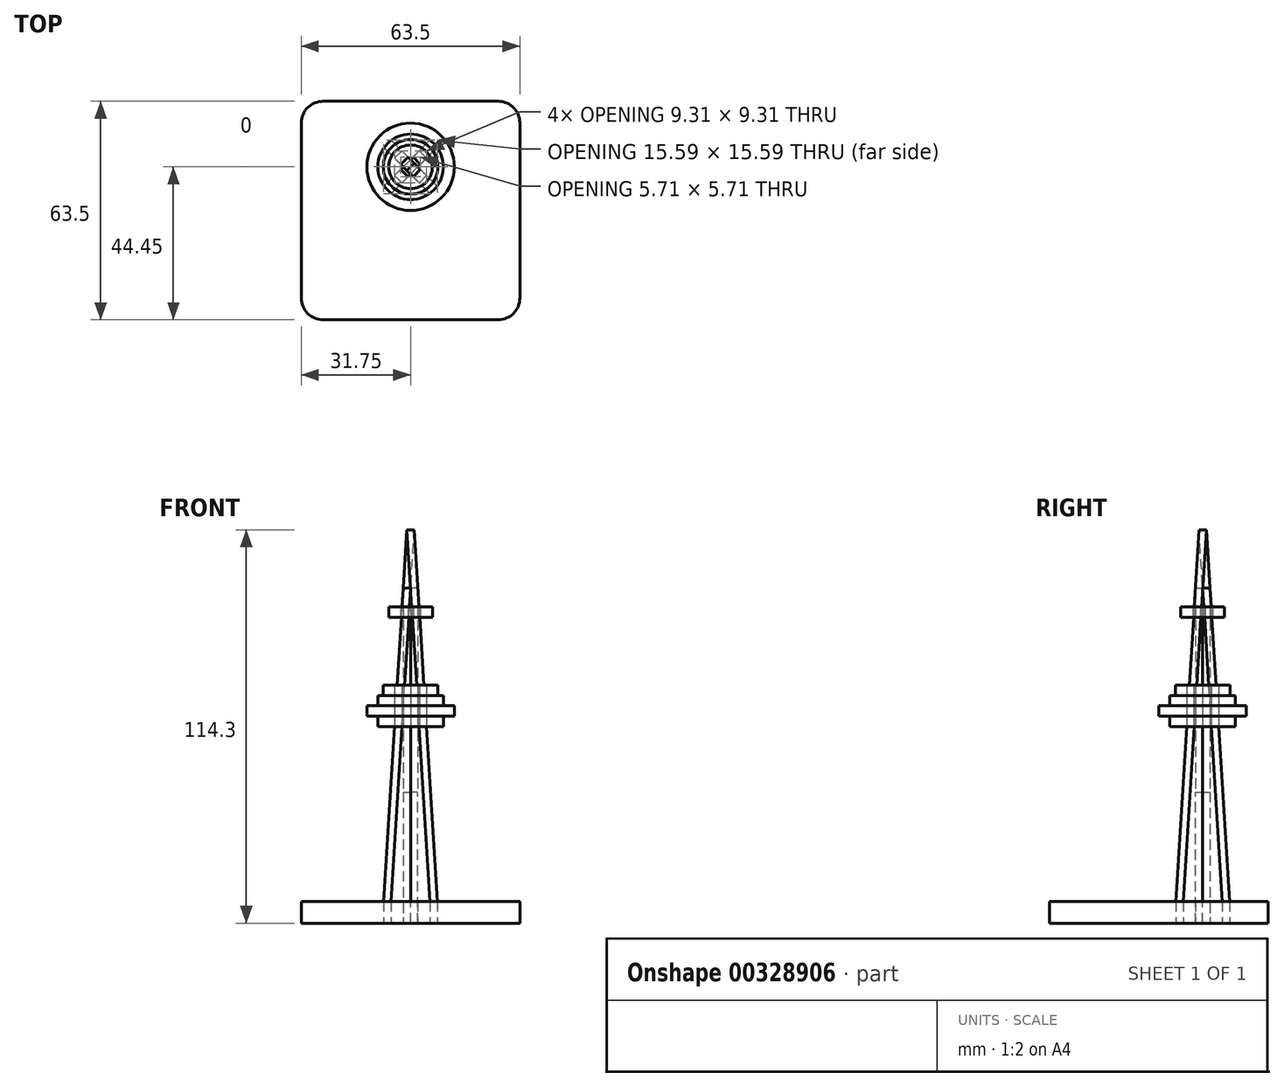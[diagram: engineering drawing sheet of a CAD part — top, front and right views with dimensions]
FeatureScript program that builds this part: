
annotation { "Feature Type Name" : "Feature", "Feature Type Description" : "" }
export const myFeature = defineFeature(function(context is Context, id is Id, definition is map)
    precondition{}
    {
        {
            var Q0;
            Q0=qCreatedBy(makeId("Top.planeOp"),FACE);
            var sketch = newSketch(context, id + "F0", { "sketchPlane" : qUnion([Q0])});
            skLineSegment(sketch, "E0", {"start": v(-7.8, 5.67) * mm, "end": v(5.67, -7.8) * mm});
            skLineSegment(sketch, "E1", {"start": v(5.67, -7.8) * mm, "end": v(7.8, -5.67) * mm});
            skLineSegment(sketch, "E2", {"start": v(7.8, -5.67) * mm, "end": v(-5.67, 7.8) * mm});
            skLineSegment(sketch, "E3", {"start": v(-7.8, 5.67) * mm, "end": v(-5.67, 7.8) * mm});
            skLineSegment(sketch, "E4", {"start": v(-7.8, 5.67) * mm, "end": v(7.8, -5.67) * mm, "construction": true});
            skLineSegment(sketch, "E5", {"start": v(-5.67, 7.8) * mm, "end": v(5.67, -7.8) * mm, "construction": true});
            skPoint(sketch, "E6", {"position": v(0, 0) * mm});
            skLineSegment(sketch, "E7", {"start": v(0, 12.63) * mm, "end": v(0, 0) * mm, "construction": true});
            skLineSegment(sketch, "E8.MirrorCS", {"start": v(-5.67, -7.8) * mm, "end": v(-7.8, -5.67) * mm});
            skLineSegment(sketch, "E9.MirrorCS", {"start": v(7.8, 5.67) * mm, "end": v(-5.67, -7.8) * mm});
            skLineSegment(sketch, "E10.MirrorCS", {"start": v(-7.8, -5.67) * mm, "end": v(5.67, 7.8) * mm});
            skLineSegment(sketch, "E11.MirrorCS", {"start": v(7.8, 5.67) * mm, "end": v(5.67, 7.8) * mm});
            skLineSegment(sketch, "E12.MirrorCS", {"start": v(5.67, 7.8) * mm, "end": v(-5.67, -7.8) * mm, "construction": true});
            skLineSegment(sketch, "E13.MirrorCS", {"start": v(7.8, 5.67) * mm, "end": v(-7.8, -5.67) * mm, "construction": true});
            skLineSegment(sketch, "E14.bottom", {"start": v(25.4, 19.05) * mm, "end": v(-25.4, 19.05) * mm});
            skLineSegment(sketch, "E14.top", {"start": v(25.4, -44.45) * mm, "end": v(-25.4, -44.45) * mm});
            skLineSegment(sketch, "E14.left", {"start": v(31.75, 12.7) * mm, "end": v(31.75, -38.1) * mm});
            skLineSegment(sketch, "E14.right", {"start": v(-31.75, 12.7) * mm, "end": v(-31.75, -38.1) * mm});
            skPoint(sketch, "E14.middle", {"position": v(0, -12.7) * mm});
            skPoint(sketch, "E15.visualSharp", {"position": v(-31.75, 19.05) * mm});
            skArc(sketch, "E15.filletArc", {"start": v(-25.4, 19.05) * mm, "mid": v(-29.9, 17.2) * mm, "end": v(-31.75, 12.7) * mm});
            skPoint(sketch, "E16.visualSharp", {"position": v(-31.75, -44.45) * mm});
            skArc(sketch, "E16.filletArc", {"start": v(-31.75, -38.1) * mm, "mid": v(-29.9, -42.6) * mm, "end": v(-25.4, -44.45) * mm});
            skPoint(sketch, "E17.visualSharp", {"position": v(31.75, -44.45) * mm});
            skArc(sketch, "E17.filletArc", {"start": v(25.4, -44.45) * mm, "mid": v(29.9, -42.6) * mm, "end": v(31.75, -38.1) * mm});
            skPoint(sketch, "E18.visualSharp", {"position": v(31.75, 19.05) * mm});
            skArc(sketch, "E18.filletArc", {"start": v(31.75, 12.7) * mm, "mid": v(29.9, 17.2) * mm, "end": v(25.4, 19.05) * mm});
            skSolve(sketch);
        }
        {
            var Q0;
            {var subQ11=sQuery(id+"F0.wireOp",EDGE,"E1");Q0=makeQuery(id+"F0.imprint","IMPRINT",FACE,{"disambiguationData":[TD([[makeQuery(id+"F0.imprint","IMPRINT",EDGE,{"derivedFrom":subQ11}),-1.0]])]});}
            extrude(context, id + "F1", {"entities" : qUnion([Q0]), "depth" : 6.35 * mm});
        }
        {
            var Q0;
            {var subQ0=sQuery(id+"F0.wireOp",EDGE,"E2");Q0=makeQuery(id+"F1.opExtrude","SWEPT_FACE",FACE,{"disambiguationData":[OSD([subQ0]),TDD([makeQuery(id+"F0.imprint","IMPRINT",EDGE,{"disambiguationData":[TD([[makeQuery(id+"F0.imprint","INTERSECT",VERTEX,{"derivedFrom":[subQ0,sQuery(id+"F0.wireOp",EDGE,"E3")]}),1.0]])],"derivedFrom":subQ0})])]});}
            var sketch = newSketch(context, id + "F2", { "sketchPlane" : qUnion([Q0])});
            skLineSegment(sketch, "E19.0", {"start": v(-9.52, 6.35) * mm, "end": v(-9.52, 0) * mm});
            skLineSegment(sketch, "E19.1", {"start": v(9.53, 6.35) * mm, "end": v(9.53, 0) * mm});
            skLineSegment(sketch, "E20", {"start": v(0, 0) * mm, "end": v(0, 114.3) * mm, "construction": true});
            skLineSegment(sketch, "E21", {"start": v(-9.52, 0) * mm, "end": v(-1.5, 0) * mm});
            skLineSegment(sketch, "E22", {"start": v(-9.52, 6.35) * mm, "end": v(0, 114.3) * mm});
            skLineSegment(sketch, "E23", {"start": v(0, 114.3) * mm, "end": v(9.52, 6.35) * mm});
            skLineSegment(sketch, "E24.0", {"start": v(-1.5, 6.35) * mm, "end": v(-1.5, 0) * mm});
            skLineSegment(sketch, "E24.1", {"start": v(1.5, 6.35) * mm, "end": v(1.5, 0) * mm});
            skLineSegment(sketch, "E25.trimOffspring", {"start": v(1.5, 0) * mm, "end": v(9.53, 0) * mm});
            skLineSegment(sketch, "E26", {"start": v(-1.5, 6.35) * mm, "end": v(-1.5, 38.1) * mm});
            skLineSegment(sketch, "E27", {"start": v(1.5, 6.35) * mm, "end": v(1.5, 38.1) * mm});
            skLineSegment(sketch, "E28", {"start": v(-1.5, 38.1) * mm, "end": v(1.5, 38.1) * mm});
            skSolve(sketch);
        }
        {
            var Q0;
            Q0 = qSketchRegion(id + "F2", true);
            extrude(context, id + "F3", {"entities" : qUnion([Q0]), "depth" : 3 * mm});
        }
        {
            var Q0;
            {var subQ0=sQuery(id+"F0.wireOp",EDGE,"E10.MirrorCS");Q0=makeQuery(id+"F1.opExtrude","SWEPT_FACE",FACE,{"disambiguationData":[OSD([subQ0]),TDD([makeQuery(id+"F0.imprint","IMPRINT",EDGE,{"disambiguationData":[TD([[makeQuery(id+"F0.imprint","INTERSECT",VERTEX,{"derivedFrom":[sQuery(id+"F0.wireOp",EDGE,"E8.MirrorCS"),subQ0]}),-1.0]])],"derivedFrom":subQ0})])]});}
            var sketch = newSketch(context, id + "F4", { "sketchPlane" : qUnion([Q0])});
            skLineSegment(sketch, "E29", {"start": v(0, 0) * mm, "end": v(0, 114.3) * mm, "construction": true});
            skLineSegment(sketch, "E30.0", {"start": v(-9.53, 6.35) * mm, "end": v(-9.53, 0) * mm});
            skLineSegment(sketch, "E30.1", {"start": v(9.52, 6.35) * mm, "end": v(9.52, 0) * mm});
            skLineSegment(sketch, "E31", {"start": v(-9.53, 0) * mm, "end": v(9.52, 0) * mm});
            skLineSegment(sketch, "E32", {"start": v(-9.52, 6.35) * mm, "end": v(-1.5, 97.3) * mm});
            skLineSegment(sketch, "E33", {"start": v(1.5, 97.3) * mm, "end": v(9.52, 6.35) * mm});
            skLineSegment(sketch, "E34.0", {"start": v(-1.5, 97.3) * mm, "end": v(-1.5, 38.1) * mm});
            skLineSegment(sketch, "E34.1", {"start": v(1.5, 97.3) * mm, "end": v(1.5, 38.1) * mm});
            skLineSegment(sketch, "E35.0", {"start": v(-1.5, 38.1) * mm, "end": v(1.5, 38.1) * mm});
            skPoint(sketch, "E36.orphan", {"position": v(-1.5, 114.3) * mm});
            skPoint(sketch, "E37.orphan", {"position": v(1.5, 114.3) * mm});
            skPoint(sketch, "E38.orphan", {"position": v(1.5, 6.35) * mm});
            skPoint(sketch, "E39.orphan", {"position": v(-1.5, 6.35) * mm});
            skSolve(sketch);
        }
        {
            var Q0;
            Q0 = qSketchRegion(id + "F4", true);
            extrude(context, id + "F5", {"entities" : qUnion([Q0]), "depth" : 3 * mm});
        }
        {
            var Q0;
            Q0=makeQuery(id+"F1.opExtrude","CAP_FACE",FACE,{"disambiguationData":[OSD([sQuery(id+"F0.wireOp",EDGE,"E0"),sQuery(id+"F0.wireOp",EDGE,"E1"),sQuery(id+"F0.wireOp",EDGE,"E2"),sQuery(id+"F0.wireOp",EDGE,"E3"),sQuery(id+"F0.wireOp",EDGE,"E8.MirrorCS"),sQuery(id+"F0.wireOp",EDGE,"E9.MirrorCS"),sQuery(id+"F0.wireOp",EDGE,"E10.MirrorCS"),sQuery(id+"F0.wireOp",EDGE,"E11.MirrorCS"),sQuery(id+"F0.wireOp",EDGE,"E14.bottom"),sQuery(id+"F0.wireOp",EDGE,"E14.top"),sQuery(id+"F0.wireOp",EDGE,"E14.left"),sQuery(id+"F0.wireOp",EDGE,"E14.right"),sQuery(id+"F0.wireOp",EDGE,"E15.filletArc"),sQuery(id+"F0.wireOp",EDGE,"E16.filletArc"),sQuery(id+"F0.wireOp",EDGE,"E17.filletArc"),sQuery(id+"F0.wireOp",EDGE,"E18.filletArc")])],"isStart":false});
            cPlane(context, id + "F6", {"entities" : qUnion([Q0]), "cplaneType" : CPlaneType.OFFSET, "offset" : 50.8 * mm, "width" : 152.4 * mm, "height" : 152.4 * mm});
        }
        {
            var Q0;
            Q0=makeQuery(id+"F1.opExtrude","CAP_FACE",FACE,{"disambiguationData":[OSD([sQuery(id+"F0.wireOp",EDGE,"E0"),sQuery(id+"F0.wireOp",EDGE,"E1"),sQuery(id+"F0.wireOp",EDGE,"E2"),sQuery(id+"F0.wireOp",EDGE,"E3"),sQuery(id+"F0.wireOp",EDGE,"E8.MirrorCS"),sQuery(id+"F0.wireOp",EDGE,"E9.MirrorCS"),sQuery(id+"F0.wireOp",EDGE,"E10.MirrorCS"),sQuery(id+"F0.wireOp",EDGE,"E11.MirrorCS"),sQuery(id+"F0.wireOp",EDGE,"E14.bottom"),sQuery(id+"F0.wireOp",EDGE,"E14.top"),sQuery(id+"F0.wireOp",EDGE,"E14.left"),sQuery(id+"F0.wireOp",EDGE,"E14.right"),sQuery(id+"F0.wireOp",EDGE,"E15.filletArc"),sQuery(id+"F0.wireOp",EDGE,"E16.filletArc"),sQuery(id+"F0.wireOp",EDGE,"E17.filletArc"),sQuery(id+"F0.wireOp",EDGE,"E18.filletArc")])],"isStart":false});
            cPlane(context, id + "F7", {"entities" : qUnion([Q0]), "cplaneType" : CPlaneType.OFFSET, "offset" : 82.55 * mm, "width" : 152.4 * mm, "height" : 152.4 * mm});
        }
        {
            var Q0;
            Q0=qCreatedBy(id+"F6.planeOp",FACE);
            var sketch = newSketch(context, id + "F8", { "sketchPlane" : qUnion([Q0])});
            skCircle(sketch, "E40", {"center": v(0, 0) * mm, "radius": 9.53 * mm});
            skLineSegment(sketch, "E41.0", {"start": v(-2.53, 4.65) * mm, "end": v(1.06, 1.06) * mm});
            skLineSegment(sketch, "E41.1", {"start": v(1.06, 1.06) * mm, "end": v(4.65, -2.53) * mm});
            skLineSegment(sketch, "E41.2", {"start": v(-1.06, -1.06) * mm, "end": v(2.53, -4.65) * mm});
            skLineSegment(sketch, "E41.3", {"start": v(-4.65, 2.53) * mm, "end": v(-1.06, -1.06) * mm});
            skLineSegment(sketch, "E41.4", {"start": v(-7.8, -5.67) * mm, "end": v(-7.71, -5.6) * mm});
            skLineSegment(sketch, "E41.5", {"start": v(-5.67, -7.8) * mm, "end": v(-5.6, -7.71) * mm});
            skLineSegment(sketch, "E41.6", {"start": v(2.12, 0) * mm, "end": v(4.65, 2.53) * mm});
            skLineSegment(sketch, "E41.7", {"start": v(0, 2.12) * mm, "end": v(2.53, 4.65) * mm});
            skPoint(sketch, "E42.orphan", {"position": v(-5.67, 7.8) * mm});
            skPoint(sketch, "E43.orphan", {"position": v(-7.8, 5.67) * mm});
            skPoint(sketch, "E44.orphan", {"position": v(7.8, -5.67) * mm});
            skPoint(sketch, "E45.orphan", {"position": v(5.67, -7.8) * mm});
            skLineSegment(sketch, "E46", {"start": v(-4.65, -2.53) * mm, "end": v(-2.53, -4.65) * mm});
            skLineSegment(sketch, "E47", {"start": v(2.53, 4.65) * mm, "end": v(4.65, 2.53) * mm});
            skLineSegment(sketch, "E48", {"start": v(-4.65, 2.53) * mm, "end": v(-2.53, 4.65) * mm});
            skLineSegment(sketch, "E49", {"start": v(2.53, -4.65) * mm, "end": v(4.65, -2.53) * mm});
            skLineSegment(sketch, "E50.trimOffspring", {"start": v(-4.65, -2.53) * mm, "end": v(-2.12, 0) * mm});
            skLineSegment(sketch, "E51.trimOffspring", {"start": v(-2.53, -4.65) * mm, "end": v(0, -2.12) * mm});
            skLineSegment(sketch, "E52.trimOffspring", {"start": v(7.71, 5.6) * mm, "end": v(7.8, 5.67) * mm});
            skLineSegment(sketch, "E53.trimOffspring", {"start": v(5.6, 7.71) * mm, "end": v(5.67, 7.8) * mm});
            skSolve(sketch);
        }
        {
            var Q0;
            {var subQ7=sQuery(id+"F8.wireOp",EDGE,"E41.6");Q0=makeQuery(id+"F8.imprint","IMPRINT",FACE,{"disambiguationData":[TD([[makeQuery(id+"F8.imprint","IMPRINT",EDGE,{"derivedFrom":subQ7}),-1.0]])]});}
            extrude(context, id + "F9", {"entities" : qUnion([Q0]), "depth" : 3 * mm});
        }
        {
            var Q0;
            Q0=makeQuery(id+"F9.opExtrude","CAP_FACE",FACE,{"disambiguationData":[OSD([sQuery(id+"F8.wireOp",EDGE,"E40"),sQuery(id+"F8.wireOp",EDGE,"E41.0"),sQuery(id+"F8.wireOp",EDGE,"E41.1"),sQuery(id+"F8.wireOp",EDGE,"E41.2"),sQuery(id+"F8.wireOp",EDGE,"E41.3"),sQuery(id+"F8.wireOp",EDGE,"E41.6"),sQuery(id+"F8.wireOp",EDGE,"E41.7"),sQuery(id+"F8.wireOp",EDGE,"E46"),sQuery(id+"F8.wireOp",EDGE,"E47"),sQuery(id+"F8.wireOp",EDGE,"E48"),sQuery(id+"F8.wireOp",EDGE,"E49"),sQuery(id+"F8.wireOp",EDGE,"E50.trimOffspring"),sQuery(id+"F8.wireOp",EDGE,"E51.trimOffspring")])],"isStart":false});
            var sketch = newSketch(context, id + "F10", { "sketchPlane" : qUnion([Q0])});
            skCircle(sketch, "E54", {"center": v(0, 0) * mm, "radius": 12.7 * mm});
            skSolve(sketch);
        }
        {
            var Q0;
            Q0=makeQuery(id+"F10.imprint","IMPRINT",FACE,{"disambiguationData":[TD([[makeQuery(id+"F10.imprint","IMPRINT",EDGE,{"derivedFrom":sQuery(id+"F10.wireOp",EDGE,"E54")}),1.0]])]});
            var Q1;
            Q1=makeQuery(id+"F10.imprint","IMPRINT",FACE,{"disambiguationData":[TD([[makeQuery(id+"F10.imprint","IMPRINT",EDGE,{"derivedFrom":makeQuery(id+"F9.opExtrude","CAP_EDGE",EDGE,{"disambiguationData":[OSD([sQuery(id+"F8.wireOp",EDGE,"E40")])],"isStart":false})}),1.0]])]});
            extrude(context, id + "F11", {"entities" : qUnion([Q0, Q1]), "depth" : 3 * mm});
        }
        {
            var Q0;
            Q0=makeQuery(id+"F11.opExtrude","CAP_FACE",FACE,{"disambiguationData":[OSD([sQuery(id+"F8.wireOp",EDGE,"E41.0"),sQuery(id+"F8.wireOp",EDGE,"E41.1"),sQuery(id+"F8.wireOp",EDGE,"E41.2"),sQuery(id+"F8.wireOp",EDGE,"E41.3"),sQuery(id+"F8.wireOp",EDGE,"E41.6"),sQuery(id+"F8.wireOp",EDGE,"E41.7"),sQuery(id+"F8.wireOp",EDGE,"E46"),sQuery(id+"F8.wireOp",EDGE,"E47"),sQuery(id+"F8.wireOp",EDGE,"E48"),sQuery(id+"F8.wireOp",EDGE,"E49"),sQuery(id+"F8.wireOp",EDGE,"E50.trimOffspring"),sQuery(id+"F8.wireOp",EDGE,"E51.trimOffspring"),sQuery(id+"F10.wireOp",EDGE,"E54")])],"isStart":false});
            var sketch = newSketch(context, id + "F12", { "sketchPlane" : qUnion([Q0])});
            skCircle(sketch, "E55", {"center": v(0, 0) * mm, "radius": 9.53 * mm});
            skSolve(sketch);
        }
        {
            var Q0;
            Q0=makeQuery(id+"F12.imprint","IMPRINT",FACE,{"disambiguationData":[TD([[makeQuery(id+"F12.imprint","IMPRINT",EDGE,{"derivedFrom":sQuery(id+"F12.wireOp",EDGE,"E55")}),1.0]])]});
            extrude(context, id + "F13", {"entities" : qUnion([Q0]), "depth" : 3 * mm});
        }
        {
            var Q0;
            Q0=makeQuery(id+"F13.opExtrude","CAP_FACE",FACE,{"disambiguationData":[OSD([sQuery(id+"F8.wireOp",EDGE,"E41.0"),sQuery(id+"F8.wireOp",EDGE,"E41.1"),sQuery(id+"F8.wireOp",EDGE,"E41.2"),sQuery(id+"F8.wireOp",EDGE,"E41.3"),sQuery(id+"F8.wireOp",EDGE,"E41.6"),sQuery(id+"F8.wireOp",EDGE,"E41.7"),sQuery(id+"F8.wireOp",EDGE,"E46"),sQuery(id+"F8.wireOp",EDGE,"E47"),sQuery(id+"F8.wireOp",EDGE,"E48"),sQuery(id+"F8.wireOp",EDGE,"E49"),sQuery(id+"F8.wireOp",EDGE,"E50.trimOffspring"),sQuery(id+"F8.wireOp",EDGE,"E51.trimOffspring"),sQuery(id+"F12.wireOp",EDGE,"E55")])],"isStart":false});
            var sketch = newSketch(context, id + "F14", { "sketchPlane" : qUnion([Q0])});
            skCircle(sketch, "E56", {"center": v(0, 0) * mm, "radius": 7.94 * mm});
            skSolve(sketch);
        }
        {
            var Q0;
            Q0=makeQuery(id+"F14.imprint","IMPRINT",FACE,{"disambiguationData":[TD([[makeQuery(id+"F14.imprint","IMPRINT",EDGE,{"derivedFrom":sQuery(id+"F14.wireOp",EDGE,"E56")}),1.0]])]});
            extrude(context, id + "F15", {"entities" : qUnion([Q0]), "depth" : 3 * mm});
        }
        {
            var Q0;
            Q0=qCreatedBy(id+"F7.planeOp",FACE);
            var sketch = newSketch(context, id + "F16", { "sketchPlane" : qUnion([Q0])});
            skCircle(sketch, "E57", {"center": v(0, 0) * mm, "radius": 6.35 * mm});
            skLineSegment(sketch, "E58.0", {"start": v(-0.74, 2.86) * mm, "end": v(0, 2.12) * mm});
            skLineSegment(sketch, "E58.1", {"start": v(2.12, 0) * mm, "end": v(2.86, -0.74) * mm});
            skLineSegment(sketch, "E58.2", {"start": v(2.12, 0) * mm, "end": v(2.86, 0.74) * mm});
            skLineSegment(sketch, "E58.3", {"start": v(0, 2.12) * mm, "end": v(0.74, 2.86) * mm});
            skLineSegment(sketch, "E58.4", {"start": v(-2.86, -0.74) * mm, "end": v(-2.12, 0) * mm});
            skLineSegment(sketch, "E58.5", {"start": v(-0.74, -2.86) * mm, "end": v(0, -2.12) * mm});
            skLineSegment(sketch, "E58.6", {"start": v(0, -2.12) * mm, "end": v(0.74, -2.86) * mm});
            skLineSegment(sketch, "E58.7", {"start": v(-2.86, 0.74) * mm, "end": v(-2.12, 0) * mm});
            skPoint(sketch, "E59.orphan", {"position": v(-5.67, 7.8) * mm});
            skPoint(sketch, "E60.orphan", {"position": v(-7.8, 5.67) * mm});
            skPoint(sketch, "E61.orphan", {"position": v(-7.8, -5.67) * mm});
            skPoint(sketch, "E62.orphan", {"position": v(-5.67, -7.8) * mm});
            skPoint(sketch, "E63.orphan", {"position": v(5.67, -7.8) * mm});
            skPoint(sketch, "E64.orphan", {"position": v(7.8, -5.67) * mm});
            skPoint(sketch, "E65.orphan", {"position": v(7.8, 5.67) * mm});
            skPoint(sketch, "E66.orphan", {"position": v(5.67, 7.8) * mm});
            skLineSegment(sketch, "E67", {"start": v(-2.86, 0.74) * mm, "end": v(-0.74, 2.86) * mm});
            skLineSegment(sketch, "E68", {"start": v(0.74, 2.86) * mm, "end": v(2.86, 0.74) * mm});
            skLineSegment(sketch, "E69", {"start": v(2.86, -0.74) * mm, "end": v(0.74, -2.86) * mm});
            skLineSegment(sketch, "E70", {"start": v(-2.86, -0.74) * mm, "end": v(-0.74, -2.86) * mm});
            skPoint(sketch, "E71.orphan", {"position": v(-1.06, -1.06) * mm});
            skPoint(sketch, "E72.orphan", {"position": v(1.06, 1.06) * mm});
            skSolve(sketch);
        }
        {
            var Q0;
            Q0=makeQuery(id+"F16.imprint","IMPRINT",FACE,{"disambiguationData":[TD([[makeQuery(id+"F16.imprint","IMPRINT",EDGE,{"derivedFrom":sQuery(id+"F16.wireOp",EDGE,"E57")}),1.0]])]});
            extrude(context, id + "F17", {"entities" : qUnion([Q0]), "depth" : 3 * mm});
        }
    });
